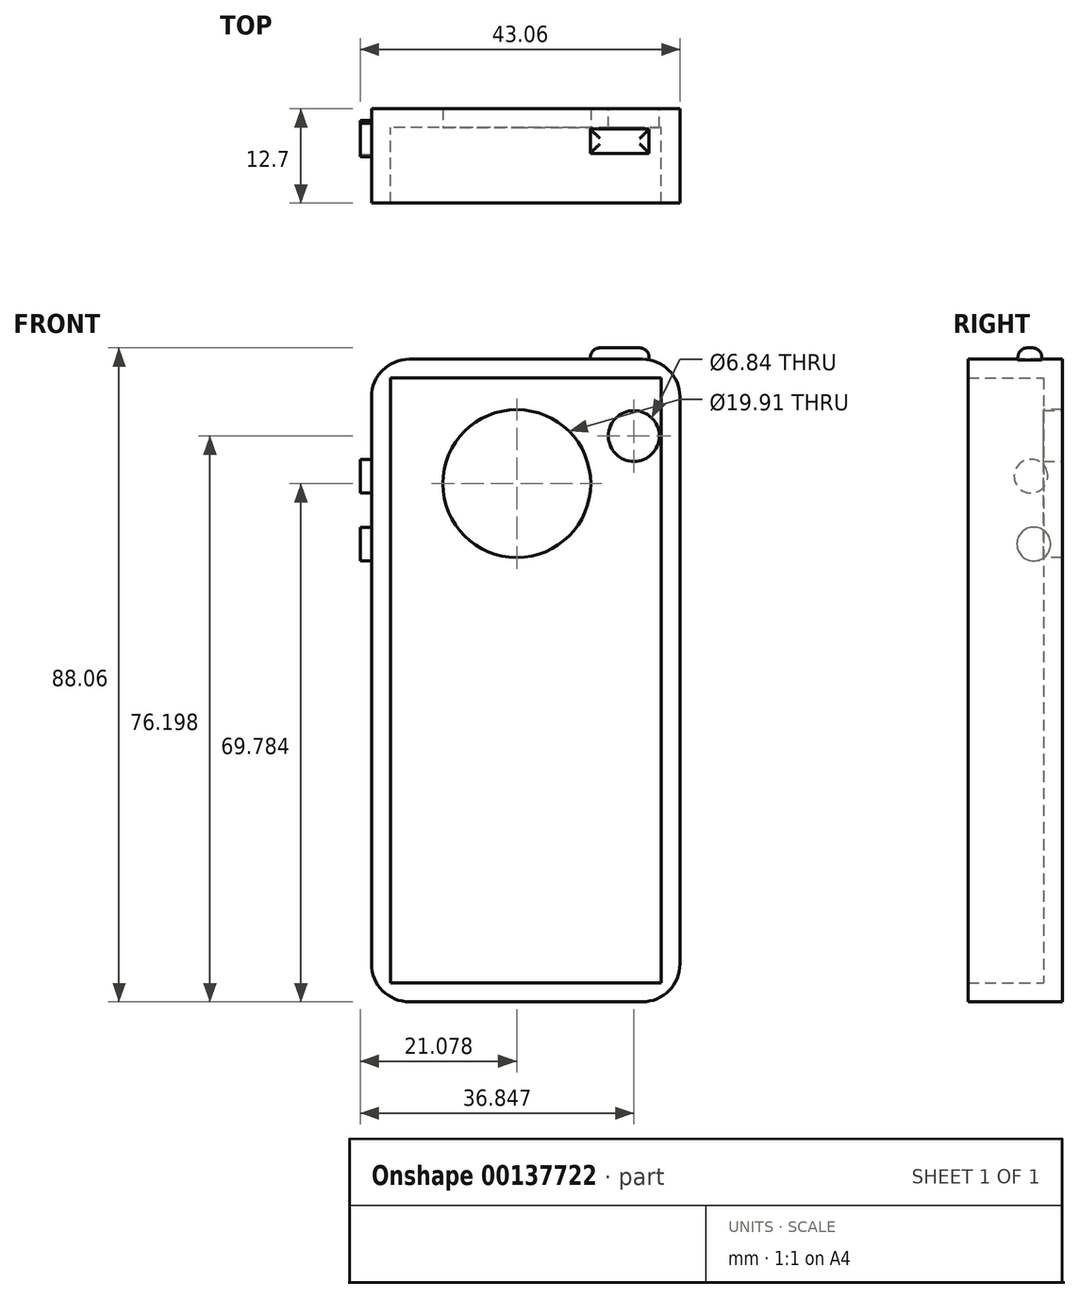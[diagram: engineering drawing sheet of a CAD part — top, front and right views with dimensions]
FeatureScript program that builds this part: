
annotation { "Feature Type Name" : "Feature", "Feature Type Description" : "" }
export const myFeature = defineFeature(function(context is Context, id is Id, definition is map)
    precondition{}
    {
        {
            var Q0;
            Q0=qCreatedBy(makeId("Front.planeOp"),FACE);
            var sketch = newSketch(context, id + "F0", { "sketchPlane" : qUnion([Q0])});
            skLineSegment(sketch, "E0.bottom", {"start": v(0, 0) * mm, "end": v(-41.54, 0) * mm});
            skLineSegment(sketch, "E0.top", {"start": v(0, -86.54) * mm, "end": v(-41.54, -86.54) * mm});
            skLineSegment(sketch, "E0.left", {"start": v(0, 0) * mm, "end": v(0, -86.54) * mm});
            skLineSegment(sketch, "E0.right", {"start": v(-41.54, 0) * mm, "end": v(-41.54, -86.54) * mm});
            skSolve(sketch);
        }
        {
            var Q0;
            Q0 = qSketchRegion(id + "F0", true);
            extrude(context, id + "F1", {"entities" : qUnion([Q0]), "depth" : 12.7 * mm});
        }
        {
            var Q0;
            Q0=makeQuery(id+"F1.opExtrude","CAP_FACE",FACE,{"disambiguationData":[OSD([sQuery(id+"F0.wireOp",EDGE,"E0.bottom"),sQuery(id+"F0.wireOp",EDGE,"E0.top"),sQuery(id+"F0.wireOp",EDGE,"E0.left"),sQuery(id+"F0.wireOp",EDGE,"E0.right")])],"isStart":false});
            shell(context, id + "F2", {"entities" : qUnion([Q0]), "thickness" : 2.54 * mm});
        }
        {
            var Q0;
            Q0=makeQuery(id+"F1.opExtrude","SWEPT_FACE",FACE,{"disambiguationData":[OSD([sQuery(id+"F0.wireOp",EDGE,"E0.right")])]});
            var sketch = newSketch(context, id + "F3", { "sketchPlane" : qUnion([Q0])});
            skCircle(sketch, "E1", {"center": v(4.21, -15.75) * mm, "radius": 2.28 * mm});
            skSolve(sketch);
        }
        {
            var Q0;
            Q0=makeQuery(id+"F3.imprint","IMPRINT",FACE,{"disambiguationData":[TD([[makeQuery(id+"F3.imprint","IMPRINT",EDGE,{"derivedFrom":sQuery(id+"F3.wireOp",EDGE,"E1")}),-1.0]])]});
            var sketch = newSketch(context, id + "F4", { "sketchPlane" : qUnion([Q0])});
            skCircle(sketch, "E2", {"center": v(3.84, -24.9) * mm, "radius": 2.27 * mm});
            skSolve(sketch);
        }
        {
            var Q0;
            Q0 = qSketchRegion(id + "F3", true);
            extrude(context, id + "F5", {"entities" : qUnion([Q0]), "operationType" : NewBodyOperationType.ADD, "depth" : 1.52 * mm});
        }
        {
            var Q0;
            Q0 = qSketchRegion(id + "F4", true);
            extrude(context, id + "F6", {"entities" : qUnion([Q0]), "operationType" : NewBodyOperationType.ADD, "depth" : 1.52 * mm});
        }
        {
            var Q0;
            Q0=makeQuery(id+"F1.opExtrude","SWEPT_FACE",FACE,{"disambiguationData":[OSD([sQuery(id+"F0.wireOp",EDGE,"E0.bottom")])]});
            var sketch = newSketch(context, id + "F7", { "sketchPlane" : qUnion([Q0])});
            skLineSegment(sketch, "E3.bottom", {"start": v(-12.07, -2.74) * mm, "end": v(-4.16, -2.74) * mm});
            skLineSegment(sketch, "E3.top", {"start": v(-12.07, -5.98) * mm, "end": v(-4.16, -5.98) * mm});
            skLineSegment(sketch, "E3.left", {"start": v(-12.07, -2.74) * mm, "end": v(-12.07, -5.98) * mm});
            skLineSegment(sketch, "E3.right", {"start": v(-4.16, -2.74) * mm, "end": v(-4.16, -5.98) * mm});
            skSolve(sketch);
        }
        {
            var Q0;
            Q0 = qSketchRegion(id + "F7", true);
            extrude(context, id + "F8", {"entities" : qUnion([Q0]), "operationType" : NewBodyOperationType.ADD, "depth" : 1.52 * mm});
        }
        {
            var Q0;
            Q0=makeQuery(id+"F8.opExtrude","CAP_FACE",FACE,{"disambiguationData":[OSD([sQuery(id+"F7.wireOp",EDGE,"E3.bottom"),sQuery(id+"F7.wireOp",EDGE,"E3.top"),sQuery(id+"F7.wireOp",EDGE,"E3.left"),sQuery(id+"F7.wireOp",EDGE,"E3.right")])],"isStart":false});
            fillet(context, id + "F9", {"entities" : qUnion([Q0]), "radius" : 1.27 * mm, "tangentPropagation" : true, "allowEdgeOverflow" : false});
        }
        {
            var Q0;
            Q0=makeQuery(id+"F1.opExtrude","SWEPT_EDGE",EDGE,{"disambiguationData":[OSD([sQuery(id+"F0.wireOp",EDGE,"E0.bottom"),sQuery(id+"F0.wireOp",EDGE,"E0.right")])]});
            fillet(context, id + "F10", {"entities" : qUnion([Q0]), "radius" : 5.08 * mm, "tangentPropagation" : true, "allowEdgeOverflow" : false});
        }
        {
            var Q0;
            Q0=makeQuery(id+"F1.opExtrude","SWEPT_EDGE",EDGE,{"disambiguationData":[OSD([sQuery(id+"F0.wireOp",EDGE,"E0.top"),sQuery(id+"F0.wireOp",EDGE,"E0.right")])]});
            fillet(context, id + "F11", {"entities" : qUnion([Q0]), "radius" : 5.08 * mm, "tangentPropagation" : true, "allowEdgeOverflow" : false});
        }
        {
            var Q0;
            Q0=makeQuery(id+"F1.opExtrude","SWEPT_EDGE",EDGE,{"disambiguationData":[OSD([sQuery(id+"F0.wireOp",EDGE,"E0.bottom"),sQuery(id+"F0.wireOp",EDGE,"E0.left")])]});
            fillet(context, id + "F12", {"entities" : qUnion([Q0]), "radius" : 5.08 * mm, "tangentPropagation" : true, "allowEdgeOverflow" : false});
        }
        {
            var Q0;
            Q0=makeQuery(id+"F1.opExtrude","SWEPT_EDGE",EDGE,{"disambiguationData":[OSD([sQuery(id+"F0.wireOp",EDGE,"E0.top"),sQuery(id+"F0.wireOp",EDGE,"E0.left")])]});
            fillet(context, id + "F13", {"entities" : qUnion([Q0]), "radius" : 5.08 * mm, "tangentPropagation" : true, "allowEdgeOverflow" : false});
        }
        {
            var Q0;
            Q0=makeQuery(id+"F1.opExtrude","CAP_FACE",FACE,{"disambiguationData":[OSD([sQuery(id+"F0.wireOp",EDGE,"E0.bottom"),sQuery(id+"F0.wireOp",EDGE,"E0.top"),sQuery(id+"F0.wireOp",EDGE,"E0.left"),sQuery(id+"F0.wireOp",EDGE,"E0.right")])],"isStart":true});
            var sketch = newSketch(context, id + "F14", { "sketchPlane" : qUnion([Q0])});
            skCircle(sketch, "E4", {"center": v(6.21, -10.34) * mm, "radius": 3.42 * mm});
            skSolve(sketch);
        }
        {
            var Q0;
            Q0 = qSketchRegion(id + "F14", true);
            extrude(context, id + "F15", {"entities" : qUnion([Q0]), "operationType" : NewBodyOperationType.REMOVE, "oppositeDirection" : true, "depth" : 37.78 * mm});
        }
        {
            var Q0;
            Q0=makeQuery(id+"F2.opShell","OFFSET_FACE",FACE,{"disambiguationData":[OSD([sQuery(id+"F0.wireOp",EDGE,"E0.bottom"),sQuery(id+"F0.wireOp",EDGE,"E0.top"),sQuery(id+"F0.wireOp",EDGE,"E0.left"),sQuery(id+"F0.wireOp",EDGE,"E0.right")])]});
            var sketch = newSketch(context, id + "F16", { "sketchPlane" : qUnion([Q0])});
            skCircle(sketch, "E5", {"center": v(-21.98, -16.76) * mm, "radius": 9.96 * mm});
            skSolve(sketch);
        }
        {
            var Q0;
            Q0 = qSketchRegion(id + "F16", true);
            extrude(context, id + "F17", {"entities" : qUnion([Q0]), "operationType" : NewBodyOperationType.REMOVE, "oppositeDirection" : true, "depth" : 26.73 * mm});
        }
    });
